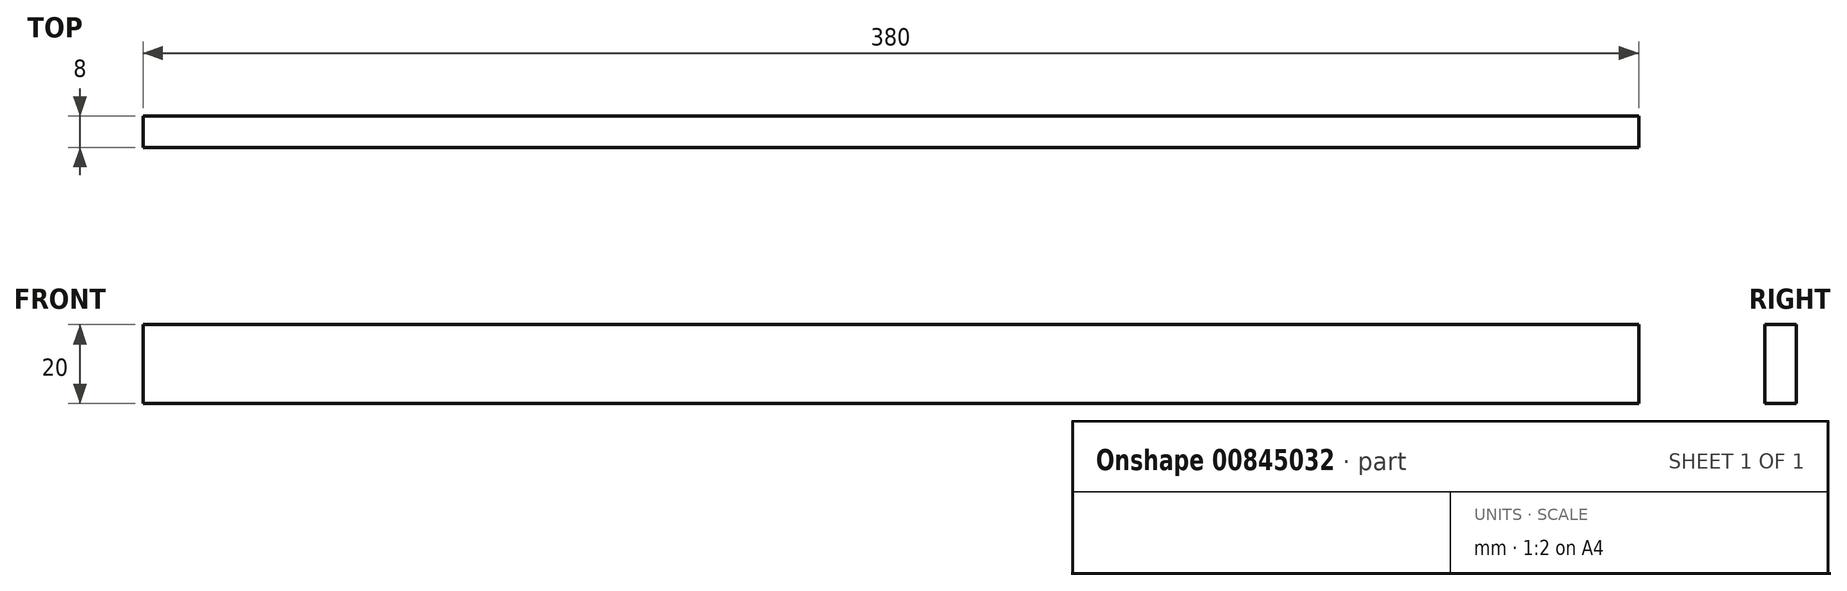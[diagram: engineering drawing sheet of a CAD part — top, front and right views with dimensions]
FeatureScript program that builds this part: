
annotation { "Feature Type Name" : "Feature", "Feature Type Description" : "" }
export const myFeature = defineFeature(function(context is Context, id is Id, definition is map)
    precondition{}
    {
        {
            var Q0;
            Q0=qCreatedBy(makeId("Front.planeOp"),FACE);
            var sketch = newSketch(context, id + "F0", { "sketchPlane" : qUnion([Q0])});
            skLineSegment(sketch, "E0.bottom", {"start": v(-190, 10) * mm, "end": v(190, 10) * mm});
            skLineSegment(sketch, "E0.top", {"start": v(-190, -10) * mm, "end": v(190, -10) * mm});
            skLineSegment(sketch, "E0.left", {"start": v(-190, 10) * mm, "end": v(-190, -10) * mm});
            skLineSegment(sketch, "E0.right", {"start": v(190, 10) * mm, "end": v(190, -10) * mm});
            skPoint(sketch, "E0.middle", {"position": v(0, 0) * mm});
            skSolve(sketch);
        }
        {
            var Q0;
            Q0=makeQuery(id+"F0.imprint","IMPRINT",FACE,{"disambiguationData":[TD([[makeQuery(id+"F0.imprint","IMPRINT",EDGE,{"derivedFrom":sQuery(id+"F0.wireOp",EDGE,"E0.bottom")}),-1.0]])]});
            extrude(context, id + "F1", {"entities" : qUnion([Q0]), "depth" : 8 * mm, "offsetDistance" : 25 * mm});
        }
    });
